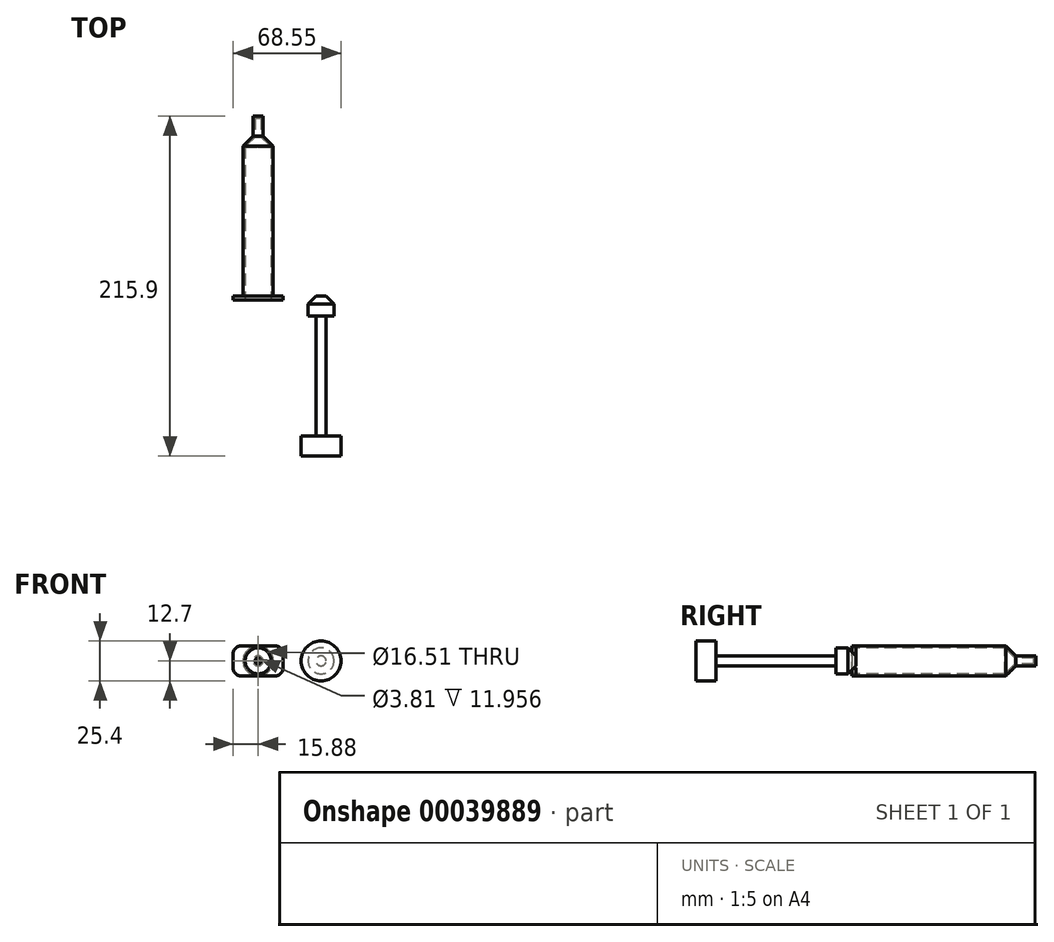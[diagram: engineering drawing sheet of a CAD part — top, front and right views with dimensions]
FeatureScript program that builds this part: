
annotation { "Feature Type Name" : "Feature", "Feature Type Description" : "" }
export const myFeature = defineFeature(function(context is Context, id is Id, definition is map)
    precondition{}
    {
        {
            var Q0;
            Q0=qCreatedBy(makeId("Front.planeOp"),FACE);
            var sketch = newSketch(context, id + "F0", { "sketchPlane" : qUnion([Q0])});
            skCircle(sketch, "E0", {"center": v(0, 0) * mm, "radius": 952.5 * mm});
            skCircle(sketch, "E1", {"center": v(0, 0) * mm, "radius": 9.52 * mm});
            skSolve(sketch);
        }
        {
            var Q0;
            Q0=makeQuery(id+"F0.imprint","IMPRINT",FACE,{"disambiguationData":[TD([[makeQuery(id+"F0.imprint","IMPRINT",EDGE,{"derivedFrom":sQuery(id+"F0.wireOp",EDGE,"E1")}),1.0]])]});
            extrude(context, id + "F1", {"entities" : qUnion([Q0]), "oppositeDirection" : true, "depth" : 101.6 * mm});
        }
        {
            var Q0;
            Q0=makeQuery(id+"F1.opExtrude","CAP_EDGE",EDGE,{"disambiguationData":[OSD([sQuery(id+"F0.wireOp",EDGE,"E1")])],"isStart":false});
            chamfer(context, id + "F2", {"entities" : qUnion([Q0]), "width" : 6.35 * mm, "tangentPropagation" : true});
        }
        {
            var Q0;
            Q0=makeQuery(id+"F1.opExtrude","CAP_FACE",FACE,{"disambiguationData":[OSD([sQuery(id+"F0.wireOp",EDGE,"E1")])],"isStart":false});
            extrude(context, id + "F3", {"entities" : qUnion([Q0]), "operationType" : NewBodyOperationType.ADD, "depth" : 12.7 * mm});
        }
        {
            var Q0;
            Q0=makeQuery(id+"F1.opExtrude","CAP_FACE",FACE,{"disambiguationData":[OSD([sQuery(id+"F0.wireOp",EDGE,"E1")])],"isStart":true});
            shell(context, id + "F4", {"entities" : qUnion([Q0]), "thickness" : 1.27 * mm});
        }
        {
            var Q0;
            Q0=makeQuery(id+"F1.opExtrude","CAP_FACE",FACE,{"disambiguationData":[OSD([sQuery(id+"F0.wireOp",EDGE,"E1")])],"isStart":true});
            var sketch = newSketch(context, id + "F5", { "sketchPlane" : qUnion([Q0])});
            skLineSegment(sketch, "E2.rect.bottom", {"start": v(-15.88, 9.53) * mm, "end": v(15.88, 9.53) * mm});
            skLineSegment(sketch, "E2.rect.top", {"start": v(-15.88, -9.52) * mm, "end": v(15.88, -9.52) * mm});
            skLineSegment(sketch, "E2.rect.left", {"start": v(-15.88, 9.53) * mm, "end": v(-15.88, -9.52) * mm});
            skLineSegment(sketch, "E2.rect.right", {"start": v(15.88, 9.53) * mm, "end": v(15.88, -9.52) * mm});
            skPoint(sketch, "E2.rect.middle", {"position": v(0, 0) * mm});
            skSolve(sketch);
        }
        {
            var Q0;
            {var subQ5=sQuery(id+"F5.wireOp",EDGE,"E2.rect.left");Q0=makeQuery(id+"F5.imprint","IMPRINT",FACE,{"disambiguationData":[TD([[makeQuery(id+"F5.imprint","IMPRINT",EDGE,{"derivedFrom":subQ5}),1.0]])]});}
            var Q1;
            {var subQ5=sQuery(id+"F5.wireOp",EDGE,"E2.rect.right");Q1=makeQuery(id+"F5.imprint","IMPRINT",FACE,{"disambiguationData":[TD([[makeQuery(id+"F5.imprint","IMPRINT",EDGE,{"derivedFrom":subQ5}),-1.0]])]});}
            var Q2;
            {var subQ0=sQuery(id+"F0.wireOp",EDGE,"E1");var subQ1=makeQuery(id+"F1.opExtrude","CAP_EDGE",EDGE,{"disambiguationData":[OSD([subQ0])],"isStart":true});Q2=makeQuery(id+"F5.imprint","IMPRINT",FACE,{"disambiguationData":[TD([[makeQuery(id+"F5.imprint","IMPRINT",EDGE,{"derivedFrom":makeQuery(id+"F4.opShell","OFFSET_EDGE",EDGE,{"disambiguationData":[OSD([subQ0]),TDD([subQ1])]})}),-1.0]])]});}
            extrude(context, id + "F6", {"entities" : qUnion([Q0, Q1, Q2]), "operationType" : NewBodyOperationType.ADD, "depth" : 2.54 * mm});
        }
        {
            var Q0;
            Q0=makeQuery(id+"F6.opExtrude","SWEPT_EDGE",EDGE,{"disambiguationData":[OSD([sQuery(id+"F5.wireOp",EDGE,"E2.rect.bottom"),sQuery(id+"F5.wireOp",EDGE,"E2.rect.left")])]});
            var Q1;
            Q1=makeQuery(id+"F6.opExtrude","SWEPT_EDGE",EDGE,{"disambiguationData":[OSD([sQuery(id+"F5.wireOp",EDGE,"E2.rect.bottom"),sQuery(id+"F5.wireOp",EDGE,"E2.rect.right")])]});
            var Q2;
            Q2=makeQuery(id+"F6.opExtrude","SWEPT_EDGE",EDGE,{"disambiguationData":[OSD([sQuery(id+"F5.wireOp",EDGE,"E2.rect.top"),sQuery(id+"F5.wireOp",EDGE,"E2.rect.right")])]});
            var Q3;
            Q3=makeQuery(id+"F6.opExtrude","SWEPT_EDGE",EDGE,{"disambiguationData":[OSD([sQuery(id+"F5.wireOp",EDGE,"E2.rect.top"),sQuery(id+"F5.wireOp",EDGE,"E2.rect.left")])]});
            fillet(context, id + "F7", {"entities" : qUnion([Q0, Q1, Q2, Q3]), "radius" : 5.08 * mm, "tangentPropagation" : true, "allowEdgeOverflow" : false});
        }
        {
            var Q0;
            Q0=qCreatedBy(makeId("Front.planeOp"),FACE);
            var sketch = newSketch(context, id + "F8", { "sketchPlane" : qUnion([Q0])});
            skCircle(sketch, "E3", {"center": v(39.97, 0) * mm, "radius": 8.26 * mm});
            skSolve(sketch);
        }
        {
            var Q0;
            Q0=makeQuery(id+"F8.imprint","IMPRINT",FACE,{"disambiguationData":[TD([[makeQuery(id+"F8.imprint","IMPRINT",EDGE,{"derivedFrom":sQuery(id+"F8.wireOp",EDGE,"E3")}),1.0]])]});
            extrude(context, id + "F9", {"entities" : qUnion([Q0]), "depth" : 12.7 * mm});
        }
        {
            var Q0;
            Q0=makeQuery(id+"F9.opExtrude","CAP_FACE",FACE,{"disambiguationData":[OSD([sQuery(id+"F8.wireOp",EDGE,"E3")])],"isStart":false});
            var sketch = newSketch(context, id + "F10", { "sketchPlane" : qUnion([Q0])});
            skCircle(sketch, "E4", {"center": v(39.97, 0) * mm, "radius": 3.18 * mm});
            skSolve(sketch);
        }
        {
            var Q0;
            Q0=makeQuery(id+"F10.imprint","IMPRINT",FACE,{"disambiguationData":[TD([[makeQuery(id+"F10.imprint","IMPRINT",EDGE,{"derivedFrom":sQuery(id+"F10.wireOp",EDGE,"E4")}),1.0]])]});
            extrude(context, id + "F11", {"entities" : qUnion([Q0]), "operationType" : NewBodyOperationType.ADD, "depth" : 76.2 * mm});
        }
        {
            var Q0;
            Q0=makeQuery(id+"F11.opExtrude","CAP_FACE",FACE,{"disambiguationData":[OSD([sQuery(id+"F10.wireOp",EDGE,"E4")])],"isStart":false});
            var sketch = newSketch(context, id + "F12", { "sketchPlane" : qUnion([Q0])});
            skCircle(sketch, "E5", {"center": v(39.97, 0) * mm, "radius": 12.7 * mm});
            skSolve(sketch);
        }
        {
            var Q0;
            Q0=makeQuery(id+"F12.imprint","IMPRINT",FACE,{"disambiguationData":[TD([[makeQuery(id+"F12.imprint","IMPRINT",EDGE,{"derivedFrom":makeQuery(id+"F11.opExtrude","CAP_EDGE",EDGE,{"disambiguationData":[OSD([sQuery(id+"F10.wireOp",EDGE,"E4")])],"isStart":false})}),1.0]])]});
            var Q1;
            Q1=makeQuery(id+"F12.imprint","IMPRINT",FACE,{"disambiguationData":[TD([[makeQuery(id+"F12.imprint","IMPRINT",EDGE,{"derivedFrom":sQuery(id+"F12.wireOp",EDGE,"E5")}),1.0]])]});
            extrude(context, id + "F13", {"entities" : qUnion([Q0, Q1]), "operationType" : NewBodyOperationType.ADD, "depth" : 12.7 * mm});
        }
        {
            var Q0;
            Q0=makeQuery(id+"F9.opExtrude","CAP_FACE",FACE,{"disambiguationData":[OSD([sQuery(id+"F8.wireOp",EDGE,"E3")])],"isStart":true});
            chamfer(context, id + "F14", {"entities" : qUnion([Q0]), "width" : 5.08 * mm, "tangentPropagation" : true});
        }
    });
